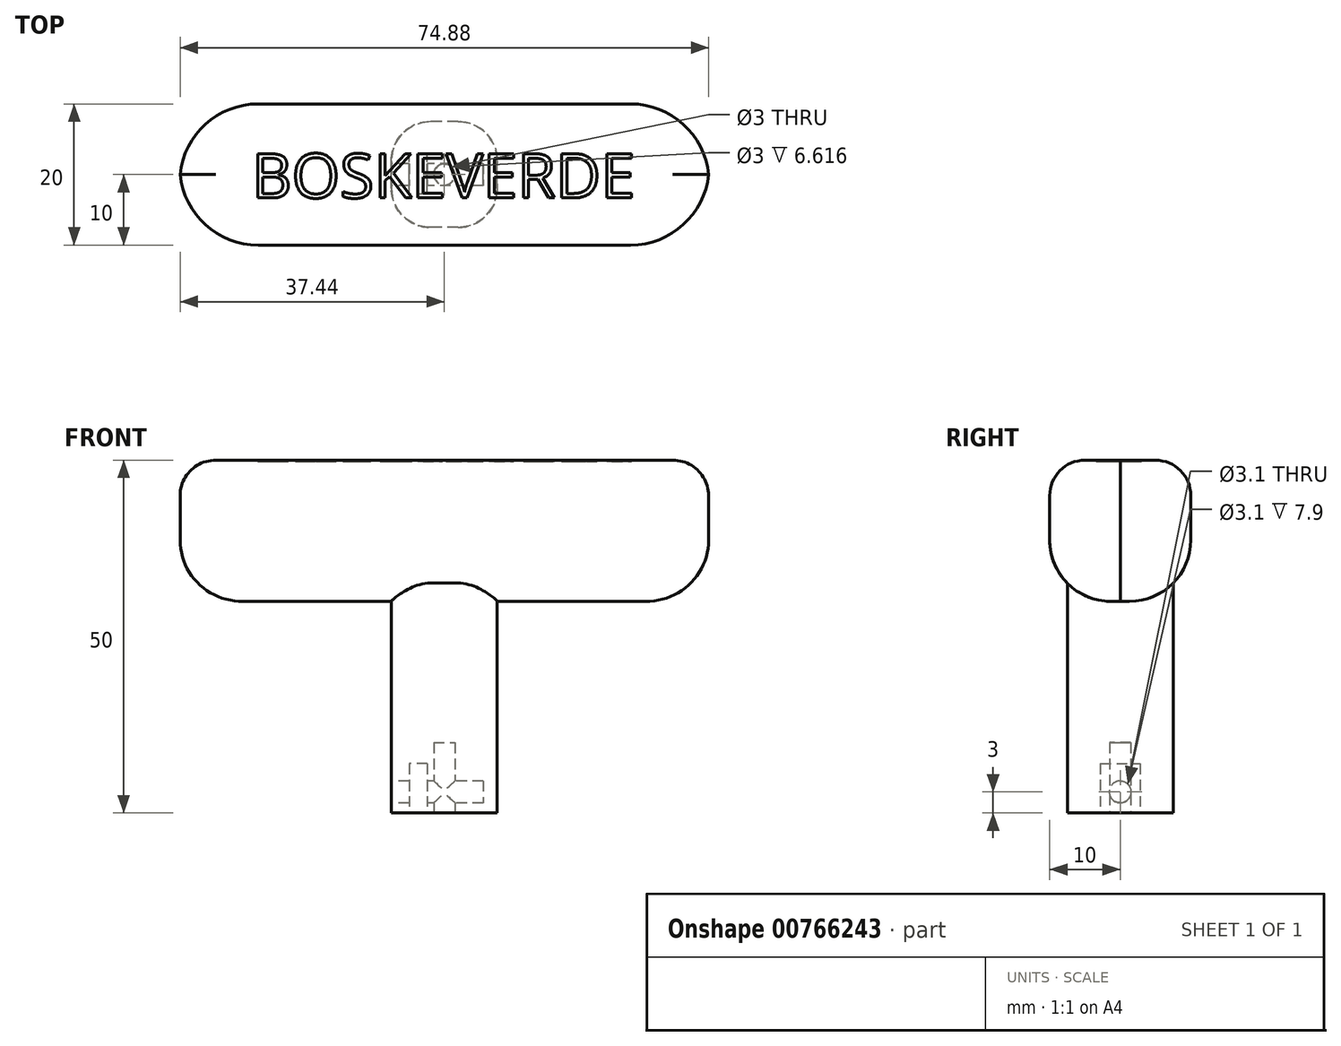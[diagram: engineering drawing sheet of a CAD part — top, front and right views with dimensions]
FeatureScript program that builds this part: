
annotation { "Feature Type Name" : "Feature", "Feature Type Description" : "" }
export const myFeature = defineFeature(function(context is Context, id is Id, definition is map)
    precondition{}
    {
        {
            var Q0;
            Q0=qCreatedBy(makeId("Front.planeOp"),FACE);
            var sketch = newSketch(context, id + "F0", { "sketchPlane" : qUnion([Q0])});
            skLineSegment(sketch, "E0", {"start": v(0, 0) * mm, "end": v(-7.5, 0) * mm});
            skLineSegment(sketch, "E1", {"start": v(-7.5, 0) * mm, "end": v(-7.5, 30) * mm});
            skLineSegment(sketch, "E2", {"start": v(-5.95, 30) * mm, "end": v(-7.5, 30) * mm});
            skLineSegment(sketch, "E3", {"start": v(-7.5, 30) * mm, "end": v(-37.5, 30) * mm});
            skLineSegment(sketch, "E4", {"start": v(-37.5, 30) * mm, "end": v(-37.5, 50) * mm});
            skLineSegment(sketch, "E5", {"start": v(-37.5, 50) * mm, "end": v(0, 50) * mm});
            skLineSegment(sketch, "E6.MirrorCS", {"start": v(37.5, 50) * mm, "end": v(0, 50) * mm});
            skLineSegment(sketch, "E7.MirrorCS", {"start": v(7.5, 30) * mm, "end": v(8.45, 30) * mm});
            skLineSegment(sketch, "E8.MirrorCS", {"start": v(0, 0) * mm, "end": v(7.5, 0) * mm});
            skLineSegment(sketch, "E9.MirrorCS", {"start": v(7.5, 0) * mm, "end": v(7.5, 30) * mm});
            skLineSegment(sketch, "E10.MirrorCS", {"start": v(37.5, 30) * mm, "end": v(37.5, 50) * mm});
            skLineSegment(sketch, "E11.MirrorCS", {"start": v(7.5, 30) * mm, "end": v(37.5, 30) * mm});
            skLineSegment(sketch, "E12", {"start": v(-7.5, 30) * mm, "end": v(7.5, 30) * mm});
            skSolve(sketch);
        }
        {
            var Q0;
            {var subQ0=sQuery(id+"F0.wireOp",EDGE,"E4");Q0=makeQuery(id+"F0.imprint","IMPRINT",FACE,{"disambiguationData":[TD([[makeQuery(id+"F0.imprint","IMPRINT",EDGE,{"derivedFrom":subQ0}),-1.0]])]});}
            extrude(context, id + "F1", {"entities" : qUnion([Q0]), "endBound" : BoundingType.SYMMETRIC, "depth" : 20 * mm, "offsetDistance" : 25 * mm});
        }
        {
            var Q0;
            Q0=makeQuery(id+"F0.imprint","IMPRINT",FACE,{"disambiguationData":[TD([[makeQuery(id+"F0.imprint","IMPRINT",EDGE,{"derivedFrom":sQuery(id+"F0.wireOp",EDGE,"E0")}),-1.0]])]});
            extrude(context, id + "F2", {"entities" : qUnion([Q0]), "operationType" : NewBodyOperationType.ADD, "endBound" : BoundingType.SYMMETRIC, "depth" : 15 * mm, "offsetDistance" : 25 * mm});
        }
        {
            var Q0;
            Q0=makeQuery(id+"F2.opExtrude","SWEPT_FACE",FACE,{"disambiguationData":[OSD([sQuery(id+"F0.wireOp",EDGE,"E0"),sQuery(id+"F0.wireOp",EDGE,"E8.MirrorCS")])]});
            var sketch = newSketch(context, id + "F3", { "sketchPlane" : qUnion([Q0])});
            skCircle(sketch, "E13", {"center": v(0, 0) * mm, "radius": 1.5 * mm});
            skSolve(sketch);
        }
        {
            var Q0;
            Q0 = qSketchRegion(id + "F3", true);
            extrude(context, id + "F4", {"entities" : qUnion([Q0]), "operationType" : NewBodyOperationType.REMOVE, "oppositeDirection" : true, "depth" : 10 * mm, "offsetDistance" : 25 * mm});
        }
        {
            var Q0;
            Q0=makeQuery(id+"F2.opExtrude","SWEPT_FACE",FACE,{"disambiguationData":[OSD([sQuery(id+"F0.wireOp",EDGE,"E0"),sQuery(id+"F0.wireOp",EDGE,"E8.MirrorCS")])]});
            var sketch = newSketch(context, id + "F5", { "sketchPlane" : qUnion([Q0])});
            skLineSegment(sketch, "E14.bottom", {"start": v(-2.4, 2.8) * mm, "end": v(-5, 2.8) * mm});
            skLineSegment(sketch, "E14.top", {"start": v(-2.4, -2.8) * mm, "end": v(-5, -2.8) * mm});
            skLineSegment(sketch, "E14.left", {"start": v(-2.4, 2.8) * mm, "end": v(-2.4, -2.8) * mm});
            skLineSegment(sketch, "E14.right", {"start": v(-5, 2.8) * mm, "end": v(-5, -2.8) * mm});
            skPoint(sketch, "E14.middle", {"position": v(-3.7, 0) * mm});
            skSolve(sketch);
        }
        {
            var Q0;
            Q0=makeQuery(id+"F5.imprint","IMPRINT",FACE,{"disambiguationData":[TD([[makeQuery(id+"F5.imprint","IMPRINT",EDGE,{"derivedFrom":sQuery(id+"F5.wireOp",EDGE,"E14.bottom")}),1.0]])]});
            extrude(context, id + "F6", {"entities" : qUnion([Q0]), "operationType" : NewBodyOperationType.REMOVE, "oppositeDirection" : true, "depth" : 7 * mm, "offsetDistance" : 25 * mm});
        }
        {
            var Q0;
            Q0=makeQuery(id+"F2.opExtrude","SWEPT_FACE",FACE,{"disambiguationData":[OSD([sQuery(id+"F0.wireOp",EDGE,"E1")])]});
            var sketch = newSketch(context, id + "F7", { "sketchPlane" : qUnion([Q0])});
            skCircle(sketch, "E15", {"center": v(0, 3) * mm, "radius": 1.55 * mm});
            skSolve(sketch);
        }
        {
            var Q0;
            Q0=makeQuery(id+"F7.imprint","IMPRINT",FACE,{"disambiguationData":[TD([[makeQuery(id+"F7.imprint","IMPRINT",EDGE,{"derivedFrom":sQuery(id+"F7.wireOp",EDGE,"E15")}),1.0]])]});
            extrude(context, id + "F8", {"entities" : qUnion([Q0]), "operationType" : NewBodyOperationType.REMOVE, "oppositeDirection" : true, "depth" : 13 * mm, "offsetDistance" : 25 * mm});
        }
        {
            var Q0;
            Q0=makeQuery(id+"F2.opExtrude","CAP_EDGE",EDGE,{"disambiguationData":[OSD([sQuery(id+"F0.wireOp",EDGE,"E1")])],"isStart":false});
            var Q1;
            Q1=makeQuery(id+"F2.opExtrude","CAP_EDGE",EDGE,{"disambiguationData":[OSD([sQuery(id+"F0.wireOp",EDGE,"E9.MirrorCS")])],"isStart":false});
            var Q2;
            Q2=makeQuery(id+"F2.opExtrude","CAP_EDGE",EDGE,{"disambiguationData":[OSD([sQuery(id+"F0.wireOp",EDGE,"E9.MirrorCS")])],"isStart":true});
            var Q3;
            Q3=makeQuery(id+"F2.opExtrude","CAP_EDGE",EDGE,{"disambiguationData":[OSD([sQuery(id+"F0.wireOp",EDGE,"E1")])],"isStart":true});
            fillet(context, id + "F9", {"entities" : qUnion([Q0, Q1, Q2, Q3]), "radius" : 5.55 * mm, "tangentPropagation" : true, "allowEdgeOverflow" : false});
        }
        {
            var Q0;
            Q0=makeQuery(id+"F1.opExtrude","CAP_EDGE",EDGE,{"disambiguationData":[OSD([sQuery(id+"F0.wireOp",EDGE,"E10.MirrorCS")])],"isStart":false});
            var Q1;
            Q1=makeQuery(id+"F1.opExtrude","CAP_EDGE",EDGE,{"disambiguationData":[OSD([sQuery(id+"F0.wireOp",EDGE,"E10.MirrorCS")])],"isStart":true});
            var Q2;
            Q2=makeQuery(id+"F1.opExtrude","CAP_EDGE",EDGE,{"disambiguationData":[OSD([sQuery(id+"F0.wireOp",EDGE,"E4")])],"isStart":false});
            var Q3;
            Q3=makeQuery(id+"F1.opExtrude","CAP_EDGE",EDGE,{"disambiguationData":[OSD([sQuery(id+"F0.wireOp",EDGE,"E4")])],"isStart":true});
            fillet(context, id + "F10", {"entities" : qUnion([Q0, Q1, Q2, Q3]), "radius" : 11.1 * mm, "tangentPropagation" : true, "allowEdgeOverflow" : false});
        }
        {
            var Q0;
            Q0=makeQuery(id+"F1.opExtrude","CAP_EDGE",EDGE,{"disambiguationData":[OSD([sQuery(id+"F0.wireOp",EDGE,"E3"),sQuery(id+"F0.wireOp",EDGE,"E11.MirrorCS"),sQuery(id+"F0.wireOp",EDGE,"E12")])],"isStart":false});
            var Q1;
            Q1=makeQuery(id+"F1.opExtrude","CAP_EDGE",EDGE,{"disambiguationData":[OSD([sQuery(id+"F0.wireOp",EDGE,"E3"),sQuery(id+"F0.wireOp",EDGE,"E11.MirrorCS"),sQuery(id+"F0.wireOp",EDGE,"E12")])],"isStart":true});
            fillet(context, id + "F11", {"entities" : qUnion([Q0, Q1]), "radius" : 8.7 * mm, "tangentPropagation" : true, "allowEdgeOverflow" : false});
        }
        {
            var Q0;
            Q0=makeQuery(id+"F1.opExtrude","SWEPT_FACE",FACE,{"disambiguationData":[OSD([sQuery(id+"F0.wireOp",EDGE,"E5"),sQuery(id+"F0.wireOp",EDGE,"E6.MirrorCS")])]});
            fillet(context, id + "F12", {"entities" : qUnion([Q0]), "radius" : 5 * mm, "tangentPropagation" : true, "allowEdgeOverflow" : false});
        }
        {
            var Q0;
            Q0=makeQuery(id+"F1.opExtrude","SWEPT_FACE",FACE,{"disambiguationData":[OSD([sQuery(id+"F0.wireOp",EDGE,"E5"),sQuery(id+"F0.wireOp",EDGE,"E6.MirrorCS")])]});
            var sketch = newSketch(context, id + "F13", { "sketchPlane" : qUnion([Q0])});
            skText(sketch, "E16", { "text": "BOSKEVERDE", "fontName": "OpenSans-Regular.ttf"});
            const initialGuessF13  = {"E16": [-0.0273, -0.00332, 1, 0, 0.00631]};
            skSetInitialGuess(sketch, initialGuessF13);
            skSolve(sketch);
        }
        {
            var Q0;
            Q0 = qSketchRegion(id + "F13", true);
            extrude(context, id + "F14", {"entities" : qUnion([Q0]), "operationType" : NewBodyOperationType.REMOVE, "oppositeDirection" : true, "depth" : 0.2 * mm, "offsetDistance" : 25 * mm});
        }
    });
